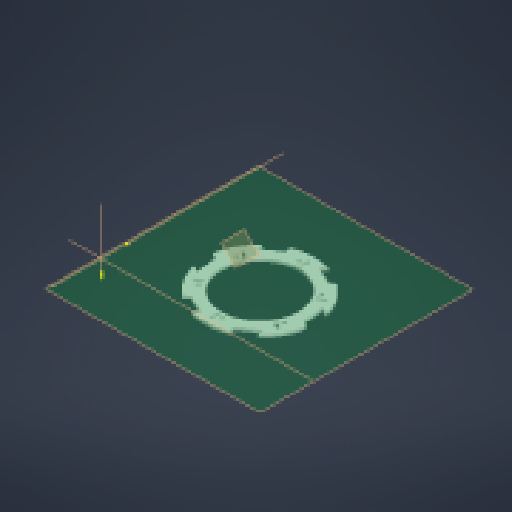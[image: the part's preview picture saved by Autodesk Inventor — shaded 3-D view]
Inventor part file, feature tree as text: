
AUTODESK INVENTOR PART (.ipt)
format: ipt  version: 2023 (Build 270158000, 158)  size: 267,776 bytes
history: native  units: mm
features: reference x25, other x13, sketch x6, extrude x3, plane x2
ambient origin geometry x8: Origin, YZ Plane, XZ Plane, XY Plane, X Axis, Y Axis, Z Axis, Center Point
bodies: Solid1 (feature_tree)
feature tree (49):
  plane  "Work Plane1"
  sketch  "Sketch1"  dims[d1=3.0mm d2=0.0mm d3=6.0mm]
  plane  "Work Plane2"
  extrude  "Extrusion1"  Depth=3.0mm
  sketch  "Sketch3"  dims[d6=4.5mm d7=4.5mm]
  extrude  "Extrusion2"  Depth=4.5mm
  sketch  "Sketch5"  dims[d9=4.5mm]
  extrude  "Extrusion3"  Depth=4.5mm
  sketch  "Sketch2"  dims[d4=4.5mm d5=4.5mm]
  reference  "Reference2"
  reference  "Reference4"
  reference  "Reference5"
  reference  "Reference6"
  reference  "Reference7"
  sketch  "Sketch4"  dims[d8=4.5mm]
  reference  "Reference8"
  reference  "Reference9"
  reference  "Reference10"
  reference  "Reference11"
  reference  "Reference12"
  reference  "Reference13"
  reference  "Reference14"
  reference  "Reference15"
  sketch  "Sketch6"  dims[d10=10.0mm d11=0.0mm d12=10.0mm d13=0.0mm]
  reference  "Reference16"
  reference  "Reference17"
  reference  "Reference18"
  reference  "Reference19"
  reference  "Reference20"
  reference  "Reference21"
  reference  "Reference22"
  reference  "Reference23"
  reference  "Reference24"
  reference  "Reference25"
  reference  "Reference26"
  reference  "Reference27"
  parser-record x1  (decoder bookkeeping rows leaked as tree rows — omitted from the tree; the rows remain in map.json)
  other  "assembly.iam"
  other  "SpantB:1"
  other  "SpantB:3"
  other  "SpantB:2"
  other  "vase:1"
  other  "ring_oben:1"
  other  "SpantA:2"
  other  "SpantA:1"
  other  "SpantA:3"
  other  "boden:1"
  other  "Assembly1"
  other  "vase_v2._tom:1"
note: 1 file-system path scrubbed to <path> (originals preserved in map.json)
